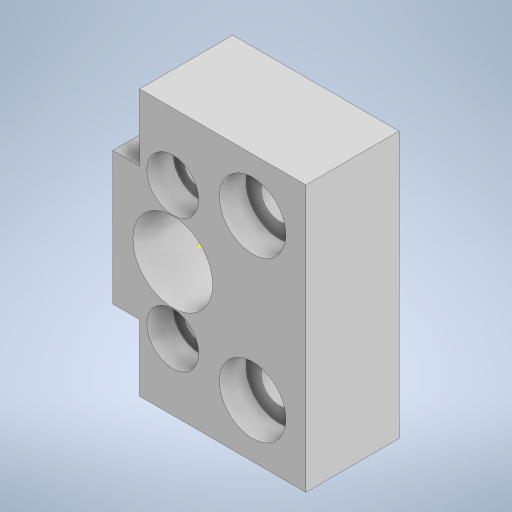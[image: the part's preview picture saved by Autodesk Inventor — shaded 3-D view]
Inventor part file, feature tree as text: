
AUTODESK INVENTOR PART (.ipt)
format: ipt  version: 2023 (Build 270158000, 158)  size: 352,768 bytes
history: native  units: mm
features: sketch x10, extrude x9, projected_geometry x4
ambient origin geometry x8: Origin, YZ Plane, XZ Plane, XY Plane, X Axis, Y Axis, Z Axis, Center Point
bodies: Solid1 (feature_tree)
feature tree (23):
  extrude  "Extrusion1"  Depth=10.0mm
  extrude  "Extrusion2"  Depth=10.0mm
  extrude  "Extrusion6"  Depth=5.0mm
  extrude  "Extrusion7"  Depth=2.4mm
  extrude  "Extrusion8"  Depth=5.0mm TaperAngle=0.0deg
  extrude  "Extrusion9"  Depth=4.0mm
  extrude  "Extrusion11"  Depth=4.0mm
  sketch  "Sketch13"  dims[d37=4.0mm d38=5.0mm]
  extrude  "Extrusion12"  Depth=5.0mm
  extrude  "Extrusion13"  Depth=5.0mm
  sketch  "Sketch1"  dims[d0=10.0mm d1=10.0mm]
  sketch  "Sketch2"  dims[d2=10.0mm d3=10.0mm]
  sketch  "Sketch7"  dims[d4=5.0mm d5=5.0mm]
  sketch  "Sketch8"  dims[d6=2.4mm d7=2.4mm]
  sketch  "Sketch9"  dims[d8=6.0mm d9=5.0mm d10=0.0mm]
  sketch  "Sketch10"  dims[d17=1.0mm d18=0.0mm d34=4.0mm]
  sketch  "Sketch12"  dims[d35=4.0mm d36=4.0mm]
  projected_geometry  "Projected Loop1"
  projected_geometry  "Projected Loop2"
  sketch  "Sketch14"  dims[d39=5.0mm d40=2.75mm]
  projected_geometry  "Projected Loop3"
  sketch  "Sketch15"  dims[d41=2.75mm d42=5.0mm d43=0.0mm d44=7.5mm d45=7.5mm d46=7.5mm d47=7.5mm d48=5.0mm d49=2.0mm d50=0.0mm d51=4.0mm d52=4.0mm d53=2.0mm d54=0.0mm d55=5.0mm d56=2.5mm d57=5.0mm d58=5.0mm d59=2.5mm d60=10.0mm d61=0.0mm d74=1.0mm d75=0.0mm d76=2.0mm d77=0.0mm d78=0.5mm d79=0.0mm d80=3.9mm d81=3.9mm]
  projected_geometry  "Projected Loop4"
